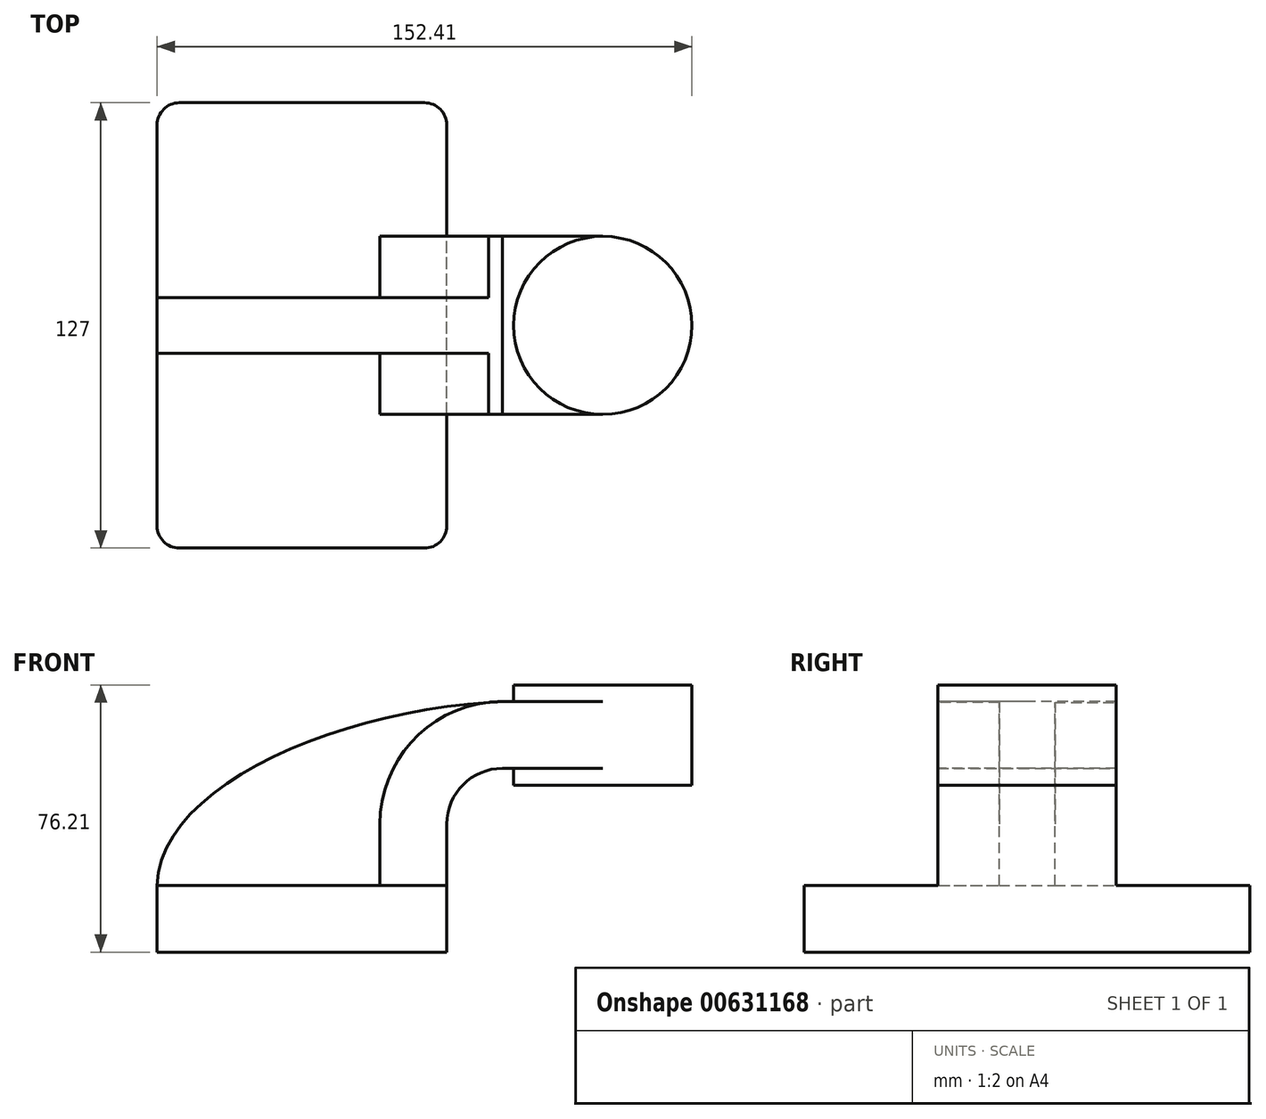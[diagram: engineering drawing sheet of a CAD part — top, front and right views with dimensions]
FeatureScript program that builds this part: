
annotation { "Feature Type Name" : "Feature", "Feature Type Description" : "" }
export const myFeature = defineFeature(function(context is Context, id is Id, definition is map)
    precondition{}
    {
        {
            var Q0;
            Q0=qCreatedBy(makeId("Front.planeOp"),FACE);
            var sketch = newSketch(context, id + "F0", { "sketchPlane" : qUnion([Q0])});
            skLineSegment(sketch, "E0.bottom", {"start": v(41.28, -9.52) * mm, "end": v(-41.28, -9.53) * mm});
            skLineSegment(sketch, "E0.top", {"start": v(41.28, 9.53) * mm, "end": v(-41.28, 9.52) * mm});
            skLineSegment(sketch, "E0.left", {"start": v(41.28, -9.52) * mm, "end": v(41.28, 9.53) * mm});
            skLineSegment(sketch, "E0.right", {"start": v(-41.28, -9.53) * mm, "end": v(-41.28, 9.52) * mm});
            skPoint(sketch, "E0.middle", {"position": v(0, 0) * mm});
            skLineSegment(sketch, "E1.bottom", {"start": v(111.12, 38.1) * mm, "end": v(60.32, 38.1) * mm});
            skLineSegment(sketch, "E1.top", {"start": v(111.12, 66.68) * mm, "end": v(60.32, 66.68) * mm});
            skLineSegment(sketch, "E1.left", {"start": v(111.12, 38.1) * mm, "end": v(111.12, 66.68) * mm});
            skLineSegment(sketch, "E1.right", {"start": v(60.32, 38.1) * mm, "end": v(60.32, 66.68) * mm});
            skPoint(sketch, "E1.middle", {"position": v(85.72, 52.39) * mm});
            skLineSegment(sketch, "E2", {"start": v(41.28, 9.53) * mm, "end": v(41.28, 27) * mm});
            skArc(sketch, "E3", {"start": v(41.28, 27) * mm, "mid": v(45.92, 38.23) * mm, "end": v(57.15, 42.88) * mm});
            skLineSegment(sketch, "E4", {"start": v(57.15, 42.88) * mm, "end": v(85.72, 42.88) * mm});
            skPoint(sketch, "E4.endSnap0", {"position": v(85.72, 38.1) * mm});
            skLineSegment(sketch, "E5.0", {"start": v(57.15, 61.93) * mm, "end": v(85.72, 61.93) * mm});
            skArc(sketch, "E5.1", {"start": v(22.23, 27) * mm, "mid": v(32.45, 51.7) * mm, "end": v(57.15, 61.93) * mm});
            skLineSegment(sketch, "E5.2", {"start": v(22.23, 9.53) * mm, "end": v(22.23, 27) * mm});
            skLineSegment(sketch, "E6", {"start": v(85.72, 38.1) * mm, "end": v(85.72, 66.68) * mm});
            skFitSpline(sketch, "E7", {"points": [v(-41.28, 9.52) * mm, v(57.15, 61.93) * mm], "startDerivative": vector(2.8, 86.8) * mm, "endDerivative": vector(137.71, 6.24) * mm});
            skSolve(sketch);
        }
        {
            var Q0;
            Q0=makeQuery(id+"F0.imprint","IMPRINT",FACE,{"disambiguationData":[TD([[makeQuery(id+"F0.imprint","IMPRINT",EDGE,{"derivedFrom":sQuery(id+"F0.wireOp",EDGE,"E0.bottom")}),-1.0]])]});
            extrude(context, id + "F1", {"entities" : qUnion([Q0]), "endBound" : BoundingType.SYMMETRIC, "depth" : 127 * mm, "offsetDistance" : 25.4 * mm});
        }
        {
            var Q0;
            {var subQ1=sQuery(id+"F0.wireOp",EDGE,"E2");Q0=makeQuery(id+"F0.imprint","IMPRINT",FACE,{"disambiguationData":[TD([[makeQuery(id+"F0.imprint","IMPRINT",EDGE,{"derivedFrom":subQ1}),1.0]])]});}
            var Q1;
            {var subQ0=sQuery(id+"F0.wireOp",EDGE,"E4");var subQ1=sQuery(id+"F0.wireOp",EDGE,"E1.right");var subQ2=makeQuery(id+"F0.imprint","INTERSECT",VERTEX,{"derivedFrom":[subQ1,subQ0]});Q1=makeQuery(id+"F0.imprint","IMPRINT",FACE,{"disambiguationData":[TD([[makeQuery(id+"F0.imprint","IMPRINT",EDGE,{"disambiguationData":[TD([[subQ2,-1.0]])],"derivedFrom":subQ1}),-1.0]])]});}
            extrude(context, id + "F2", {"entities" : qUnion([Q0, Q1]), "operationType" : NewBodyOperationType.ADD, "endBound" : BoundingType.SYMMETRIC, "depth" : 50.8 * mm, "offsetDistance" : 25.4 * mm});
        }
        {
            var Q0;
            {var subQ3=sQuery(id+"F0.wireOp",EDGE,"E5.2");Q0=makeQuery(id+"F0.imprint","IMPRINT",FACE,{"disambiguationData":[TD([[makeQuery(id+"F0.imprint","IMPRINT",EDGE,{"derivedFrom":subQ3}),1.0]])]});}
            extrude(context, id + "F3", {"entities" : qUnion([Q0]), "operationType" : NewBodyOperationType.ADD, "endBound" : BoundingType.SYMMETRIC, "depth" : 15.88 * mm, "offsetDistance" : 25.4 * mm});
        }
        {
            var Q0;
            {var subQ0=sQuery(id+"F0.wireOp",EDGE,"E1.left");Q0=makeQuery(id+"F0.imprint","IMPRINT",FACE,{"disambiguationData":[TD([[makeQuery(id+"F0.imprint","IMPRINT",EDGE,{"derivedFrom":subQ0}),1.0]])]});}
            var Q1;
            Q1=sQuery(id+"F0.wireOp",EDGE,"E6");
            revolve(context, id + "F4", {"operationType" : NewBodyOperationType.ADD, "entities" : qUnion([Q0]), "axis" : qUnion([Q1]), "revolveType" : RevolveType.FULL});
        }
        {
            var Q0;
            Q0=makeQuery(id+"F1.opExtrude","CAP_EDGE",EDGE,{"disambiguationData":[OSD([sQuery(id+"F0.wireOp",EDGE,"E0.left")])],"isStart":false});
            var Q1;
            Q1=makeQuery(id+"F1.opExtrude","CAP_EDGE",EDGE,{"disambiguationData":[OSD([sQuery(id+"F0.wireOp",EDGE,"E0.right")])],"isStart":false});
            var Q2;
            Q2=makeQuery(id+"F1.opExtrude","CAP_EDGE",EDGE,{"disambiguationData":[OSD([sQuery(id+"F0.wireOp",EDGE,"E0.left")])],"isStart":true});
            var Q3;
            Q3=makeQuery(id+"F1.opExtrude","CAP_EDGE",EDGE,{"disambiguationData":[OSD([sQuery(id+"F0.wireOp",EDGE,"E0.right")])],"isStart":true});
            fillet(context, id + "F5", {"entities" : qUnion([Q0, Q1, Q2, Q3]), "radius" : 6.35 * mm, "tangentPropagation" : true, "allowEdgeOverflow" : false});
        }
    });
